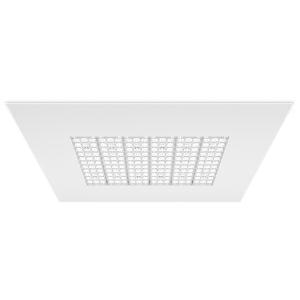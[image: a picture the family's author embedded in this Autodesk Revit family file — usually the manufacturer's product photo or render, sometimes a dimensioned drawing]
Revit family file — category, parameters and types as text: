
# Revit family: 3f_filippi_-_3f_six_r_ugr_3f_filippi_-_22245_-_3f_six_r_40-840_dali_ugr_596x596
name_source: partatom
category: Lighting Fixtures
units: mm (PartAtom-declared; Revit-internal decimal feet)

## family parameters
Cut with Voids When Loaded = No
Host = Face
Light Source = No
Part Type = Normal
Room Calculation Point = No
Round Connector Dimension = Use Diameter
Shared = No

## types (1)
- 3F Filippi - 3F Six R UGR (1 x LED, 6621 lm, 40 W, 4000 K)
    Apparent Load = 40 VA
    Approval mark = ENEC
    CIE Flux Codes = 83 96 99 100 100
    Color Rendering = 80
    Color Temperature = 4000 K
    Control Gear = Electronic transformer
    Default Elevation = 1800 mm
    Description = ILLUMINOTECHNICAL
Luminous efficiency 100% (DLOR 100%, ULOR 0%).
Initial luminous flux of the luminaire 6621 lm.
Direct symmetric distribution.
Installation Interdistance Transv.D = 1.39 x hu - Long.D = 1.30 x hu.
Average luminance <3000 cd/m² for radial angles >65°.
Tabular UGR (CIE 117 - 4H-8H; S=0.25H; 70/50/20): RUG 19.5 - 17.2.
Beam angle: 78° - 75°.
Luminous efficacy 166 lm/W.
Lifetime (L93/B10): 30000 h. (tq+25°C)
Lifetime (L90/B10): 50000 h. (tq+25°C)
Lifetime (L85/B10): 80000 h. (tq+25°C)
Lifetime (L80/B10): 100000 h. (tq+25°C)
Lifetime (L85/B10): 50000 h. (tq+50°C)
Sudden decreased luminous flux after 50000 hours: 0% (C0).
Photobiological safety in compliance with IEC/TR 62778: RG0 risk exempt, (IEC 62471).
In compliance with IEC/EN 62722-2-1 - IEC/EN 62717 standards.

SOURCE
Linear LED module 40W/840.
Energy efficiency class (UE 2019/2020 - UE 2019/2015): C.
CIE 13.3 Colour rendering index: CRI >80 (R9 <50%).
IES TM-30 Fidelity Index: Rf = 84 Rg = 95.
CCT nominal colour temperature 4000 K.
Colour initial tolerance (MacAdam): SDCM 3.

MECHANICAL
Housing in galvannealed steel, painted in white epoxy-polyester.
Methacrylate (PMMA) lenses with external flat surface.
Luminaire with limited surface temperature. - D - (EN 60598-2-24)
Dimensions: 596x596 mm, height 70 mm. Weight 4.6 kg.
IP40 protection degree.
Mechanical strength to impacts IK06 (1 joule).
Glow-wire test resistance 650°C.

ELECTRICAL
Halogen Free DALI-2, PUSH-DIM, electronic wiring 230V-50/60Hz, power factor 0.95 at full load, THD <25%, constant output current, class I, 1 driver, 1 DALI addresse.
Power of the luminaire 40 W.
CE - IEC 60598-1 - EN 60598-1.
SAFE FLICKER: PstLM=<1 and SVM=<0.4 (IEC TR 61547-1 and IEC TR 63158), to ensure a more comfortable and safe light.
Luminaire compliant with EN 60598-2-22 for power supply from a centralised emergency system CPSS (Central Power Supply System), not incorporated in the luminaire - high risk areas excluded. The default power and flux are 100% in AC and 15% in DC.
Ambient temperature from 0°C to +50°C.
Temperature class T6 max 85°C.
Power cable type H05Z1Z1-F 5x1.5 mm² that protrudes by 1 m with sheared ends.
Relative humidity UR: <85%.

INSTALLATION
Lay-in recessed fitting.
All accessories dedicated to this product are available on the Catalog and on our website www.3F-Filippi.com.

APPLICATIONS
Suitable product for food production plants (HACCP), IFS (Food Version 6), BRC (GSFS Food Version 7).
Environments: commercial, exhibition areas, transit areas, lobbies or waiting rooms, shops.
Environments that need luminance control.

LIGHT MANAGEMENT
Recommended minimum setting: 10%.
The device, equipped with DALI-2 driver, can be controlled manually with 3F Easy Dim technology or automatically/manually with 3F Smart Dimming technology and/or centralised DALI systems.
DALI-2 certification guarantees interoperability with other devices with the same certification.
In electrical systems without a regulation system (manual or automatic) and DALI bus, a suitable jumper must be made on the DA-DA terminals of the appliance.

WARNING
Luminaire designed for disposal/recycling at end-of-life.
Replaceable (LED only) light source by a professional. Replaceable control gear by a professional.
    Height = 0 mm  [stored 0 ft]
    Lamp = 1 x LED
    Lamp Light Flux = 6621 lm
    Lamp Power = 40 W
    Lamp count = 1
    Length = 596 mm
    Lifetime = 50000 h
    Luminous efficacy = 166 lm/W
    Manufacturer = 3F Filippi
    ModVariant = No
    Model = 3F Filippi - 22245 - 3F Six R 40-840 DALI UGR 596x596
    Mounting Place = Ceiling
    Mounting Type = Recessed
    Number of Poles = 1
    OnlyDefault = Yes
    Power Factor = 1
    Product Name = 3F Filippi - 3F Six R UGR
    Product group = recessed luminaire
    ProductGroupID = 4
    Protection Class = Protection class I
    Protection Degree = IP 40
    RLX_Detail_Level = 1
    RLX_Emergency_Light_Flux = 0 lm
    RLX_Emergency_Type = 0
    RLX_Emergency_Type_DB = No
    RlxData = <blob elided: 136757 chars, md5=0cc3697a>
    Socket = socket
    Standby Power = 0 W
    System Light Flux = 6621 lm
    System Power = 40 W
    Type Comments = Product without accessories
    Type Image = 3ffilippi_3f_six_r_ugr.jpg
    URL = http://relux.com
    VarID = ---
    Voltage = 0 V
    Weight = 0.00 kg
    Width = 596 mm

note: [stored X ft] marks values corroborated as IEEE doubles in the binary element streams (Revit-internal decimal feet)

## geometry (parser evidence)
native form markers: Blend x4, Sweep x10
no freeform markers — native parametric forms only
